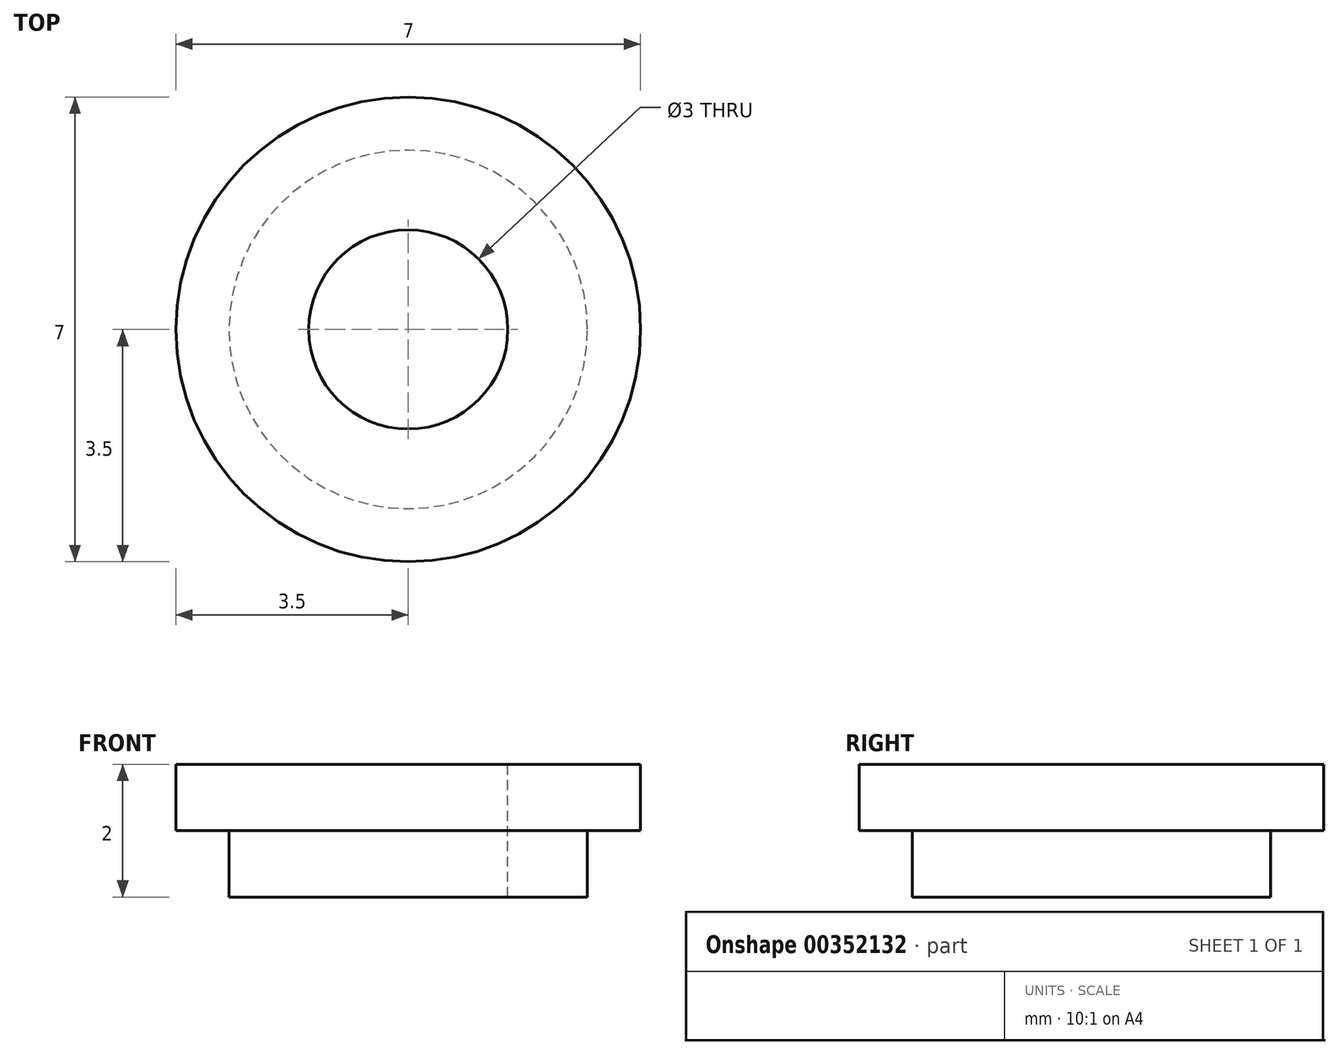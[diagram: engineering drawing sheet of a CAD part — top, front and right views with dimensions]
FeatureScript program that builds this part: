
annotation { "Feature Type Name" : "Feature", "Feature Type Description" : "" }
export const myFeature = defineFeature(function(context is Context, id is Id, definition is map)
    precondition{}
    {
        {
            var Q0;
            Q0=qCreatedBy(makeId("Front.planeOp"),FACE);
            var sketch = newSketch(context, id + "F0", { "sketchPlane" : qUnion([Q0])});
            skLineSegment(sketch, "E0", {"start": v(0, 9.29) * mm, "end": v(0, 0.61) * mm});
            skLineSegment(sketch, "E1", {"start": v(-1.5, 0) * mm, "end": v(-1.5, 2) * mm});
            skLineSegment(sketch, "E2", {"start": v(-1.5, 2) * mm, "end": v(-3.5, 2) * mm});
            skLineSegment(sketch, "E3", {"start": v(-3.5, 2) * mm, "end": v(-3.5, 1) * mm});
            skLineSegment(sketch, "E4", {"start": v(-3.5, 1) * mm, "end": v(-2.7, 1) * mm});
            skLineSegment(sketch, "E5", {"start": v(-2.7, 1) * mm, "end": v(-2.7, 0) * mm});
            skLineSegment(sketch, "E6", {"start": v(-2.7, 0) * mm, "end": v(-1.5, 0) * mm});
            skSolve(sketch);
        }
        {
            var Q0;
            Q0 = qSketchRegion(id + "F0", true);
            var Q1;
            Q1=sQuery(id+"F0.wireOp",EDGE,"E0");
            revolve(context, id + "F1", {"entities" : qUnion([Q0]), "axis" : qUnion([Q1]), "revolveType" : RevolveType.FULL});
        }
    });
